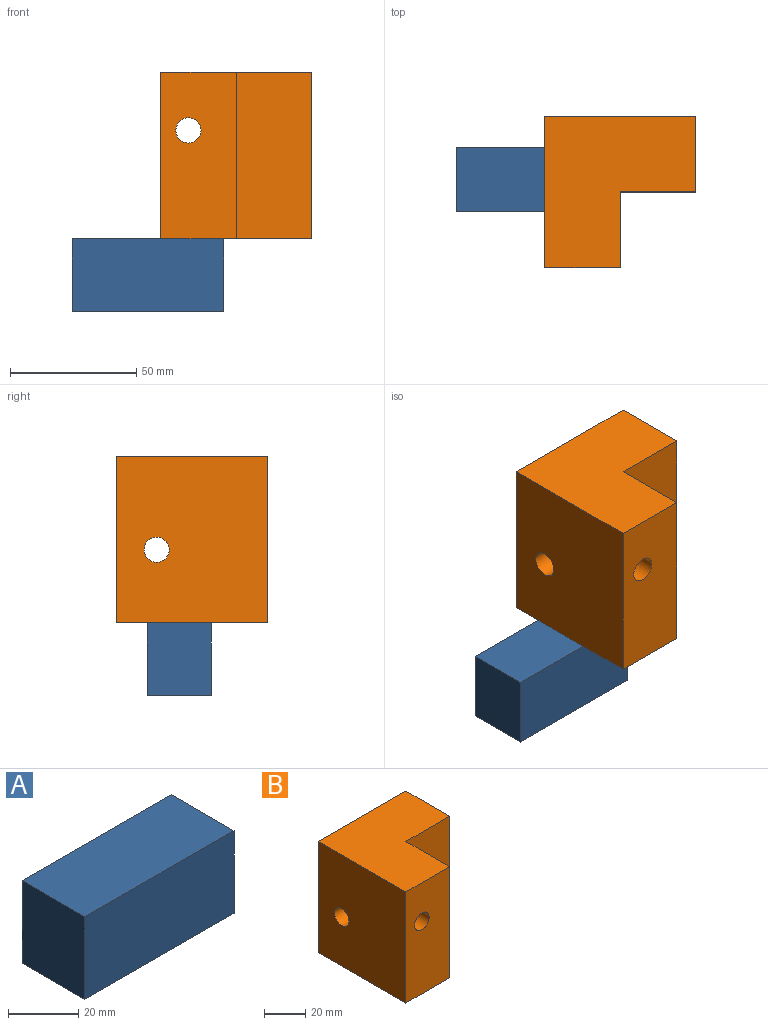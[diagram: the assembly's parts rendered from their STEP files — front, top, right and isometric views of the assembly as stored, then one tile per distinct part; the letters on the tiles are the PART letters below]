
ASSEMBLY  parts=2 mates=1
PART A: 6 faces, bbox 60.2x25.4x28.9 mm
  f0: plane 60.21x25.4mm, normal (0,0,1), area 1529.4mm2, adj f1,f3,f4,f5
  f1: plane 28.87x25.4mm, normal (-1,0,0), area 733.2mm2, adj f0,f2,f4,f5
  f2: plane 60.21x25.4mm, normal (0,0,-1), area 1529.4mm2, adj f1,f3,f4,f5
  f3: plane 28.87x25.4mm, normal (1,0,0), area 733.2mm2, adj f0,f2,f4,f5
  f4: plane 60.21x28.87mm, normal (0,-1,0), area 1738.2mm2, adj f0,f1,f2,f3
  f5: plane 60.21x28.87mm, normal (0,1,0), area 1738.2mm2, adj f0,f1,f2,f3
PART B: 10 faces, bbox 60x60x66 mm
  f0: plane 66x30mm, normal (1,0,0), area 1901.5mm2, adj f2,f3,f4,f8,f9
  f1: plane 66x30mm, normal (0,-1,0), area 1901.5mm2, adj f2,f3,f5,f6,f7
  f2: plane 60x60mm, normal (0,0,1), area 2700mm2, adj f0,f1,f4,f5,f7,f8
  f3: plane 60x60mm, normal (0,0,-1), area 2700mm2, adj f0,f1,f4,f5,f7,f8
  f4: plane 66x60mm, normal (0,1,0), area 3881.5mm2, adj f0,f2,f3,f5,f6
  f5: plane 66x60mm, normal (-1,0,0), area 3881.5mm2, adj f1,f2,f3,f4,f9
  f6: cylinder r=5mm len=60mm, axis (0,-1,0), area 1885mm2, adj f1,f4
  f7: plane 66x30mm, normal (1,0,0), area 1980mm2, adj f1,f2,f3,f8
  f8: plane 66x30mm, normal (0,-1,0), area 1980mm2, adj f0,f2,f3,f7
  f9: cylinder r=5mm len=60mm, axis (-1,0,0), area 1885mm2, adj f0,f5
PLACE A t=(-52.49,14.63,-38.25)mm
PLACE B t=(-13.68,-3.07,-24.27)mm
MATE planar A.f0 <-> B.f3  axis (0,0,1) through (-18.68,1.93,-24.27)mm
